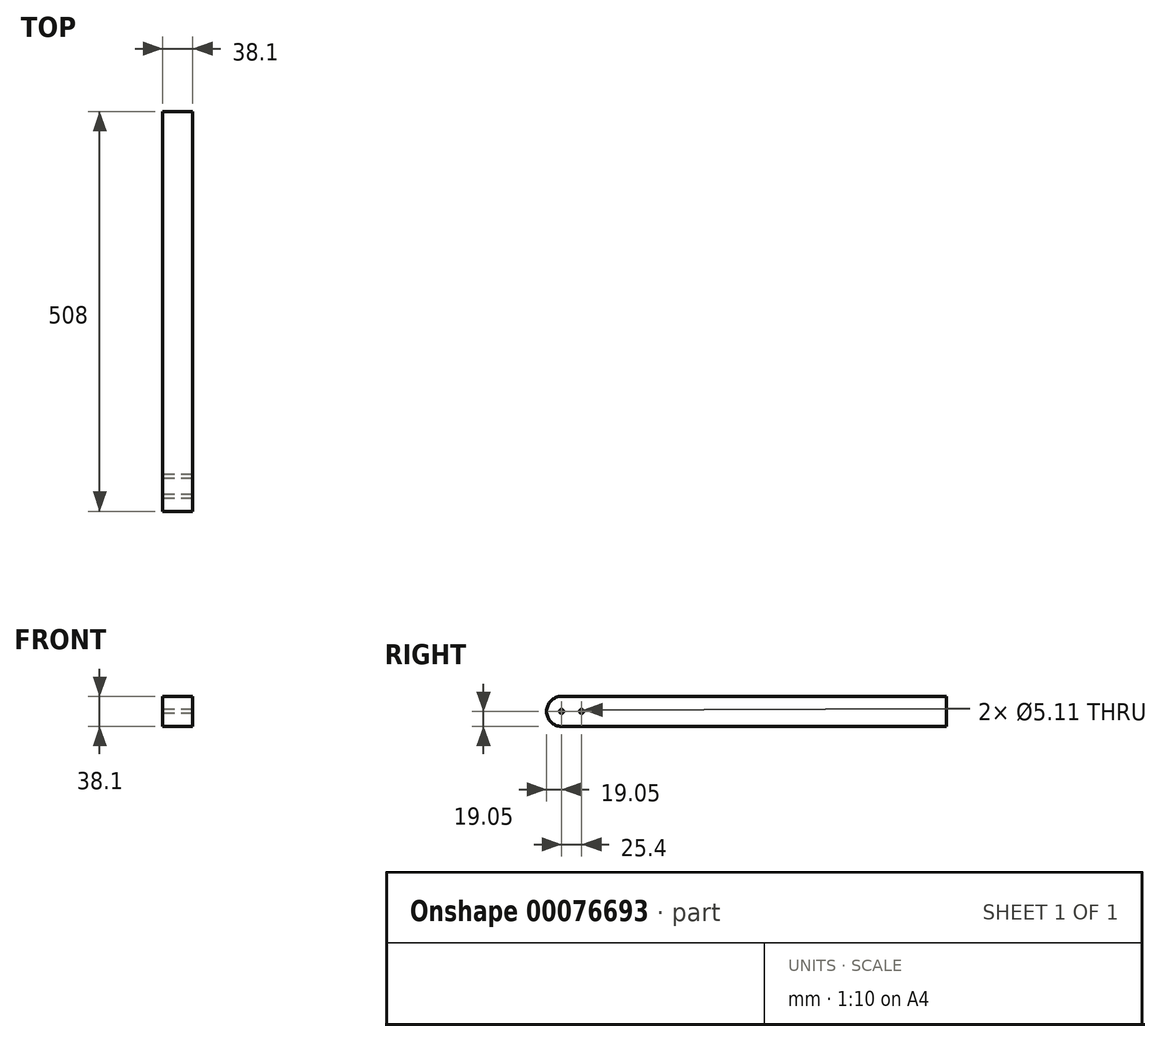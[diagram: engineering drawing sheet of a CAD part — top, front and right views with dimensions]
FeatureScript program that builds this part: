
annotation { "Feature Type Name" : "Feature", "Feature Type Description" : "" }
export const myFeature = defineFeature(function(context is Context, id is Id, definition is map)
    precondition{}
    {
        {
            var Q0;
            Q0=qCreatedBy(makeId("Front.planeOp"),FACE);
            var sketch = newSketch(context, id + "F0", { "sketchPlane" : qUnion([Q0])});
            skLineSegment(sketch, "E0.bottom", {"start": v(0, 0) * mm, "end": v(-38.1, 0) * mm});
            skLineSegment(sketch, "E0.top", {"start": v(0, 38.1) * mm, "end": v(-38.1, 38.1) * mm});
            skLineSegment(sketch, "E0.left", {"start": v(0, 0) * mm, "end": v(0, 38.1) * mm});
            skLineSegment(sketch, "E0.right", {"start": v(-38.1, 0) * mm, "end": v(-38.1, 38.1) * mm});
            skSolve(sketch);
        }
        {
            var Q0;
            Q0=makeQuery(id+"F0.imprint","IMPRINT",FACE,{"disambiguationData":[TD([[makeQuery(id+"F0.imprint","IMPRINT",EDGE,{"derivedFrom":sQuery(id+"F0.wireOp",EDGE,"E0.bottom")}),-1.0]])]});
            extrude(context, id + "F1", {"entities" : qUnion([Q0]), "depth" : 508 * mm});
        }
        {
            var Q0;
            Q0=makeQuery(id+"F1.opExtrude","CAP_EDGE",EDGE,{"disambiguationData":[OSD([sQuery(id+"F0.wireOp",EDGE,"E0.top")])],"isStart":false});
            var Q1;
            Q1=makeQuery(id+"F1.opExtrude","CAP_EDGE",EDGE,{"disambiguationData":[OSD([sQuery(id+"F0.wireOp",EDGE,"E0.bottom")])],"isStart":false});
            fillet(context, id + "F2", {"entities" : qUnion([Q0, Q1]), "radius" : 19.05 * mm, "tangentPropagation" : true, "allowEdgeOverflow" : false});
        }
        {
            var Q0;
            Q0=makeQuery(id+"F1.opExtrude","SWEPT_FACE",FACE,{"disambiguationData":[OSD([sQuery(id+"F0.wireOp",EDGE,"E0.right")])]});
            var sketch = newSketch(context, id + "F3", { "sketchPlane" : qUnion([Q0])});
            skLineSegment(sketch, "E1.0", {"start": v(488.95, 19.05) * mm, "end": v(0, 19.05) * mm, "construction": true});
            skLineSegment(sketch, "E2.0", {"start": v(488.95, 19.05) * mm, "end": v(488.95, 19.05) * mm});
            skCircle(sketch, "E3", {"center": v(488.95, 19.05) * mm, "radius": 2.55 * mm, "construction": true});
            skCircle(sketch, "E4", {"center": v(463.55, 19.05) * mm, "radius": 2.55 * mm});
            skSolve(sketch);
        }
        {
            var Q0;
            Q0=sQuery(id+"F3.wireOp",VERTEX,"E1.0.start");
            var Q1;
            Q1=sQuery(id+"F3.wireOp",VERTEX,"E4.center");
            var Q2;
            Q2=makeQuery(id+"F1.opExtrude","SWEPT_BODY",BODY,{"disambiguationData":[OSD([sQuery(id+"F0.wireOp",EDGE,"E0.bottom"),sQuery(id+"F0.wireOp",EDGE,"E0.top"),sQuery(id+"F0.wireOp",EDGE,"E0.left"),sQuery(id+"F0.wireOp",EDGE,"E0.right")])]});
            hole(context, id + "F4", {"style" : HoleStyle.SIMPLE, "endStyle" : HoleEndStyle.THROUGH, "holeDiameter" : 5.1 * mm, "locations" : qUnion([Q0, Q1]), "scope" : qUnion([Q2]), "isTappedThrough" : true});
        }
    });
